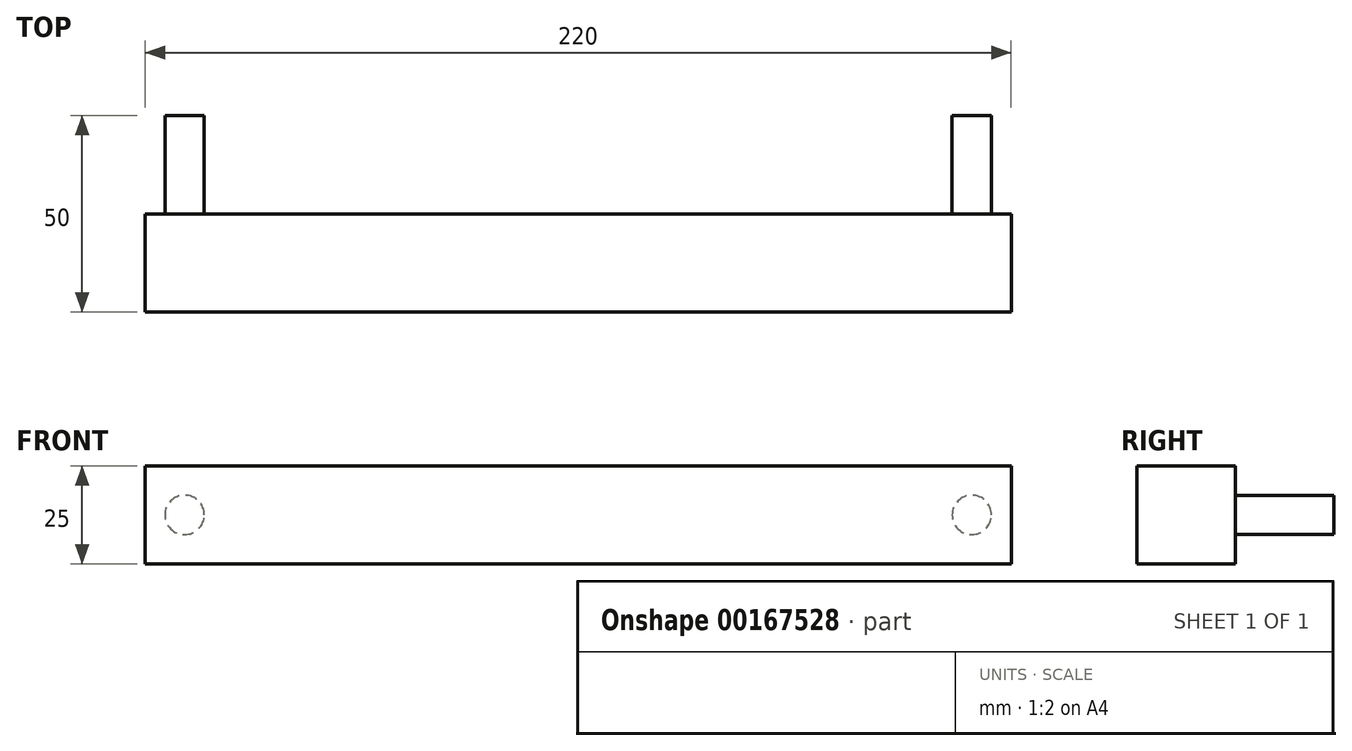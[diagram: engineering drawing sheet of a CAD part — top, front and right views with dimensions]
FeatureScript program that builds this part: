
annotation { "Feature Type Name" : "Feature", "Feature Type Description" : "" }
export const myFeature = defineFeature(function(context is Context, id is Id, definition is map)
    precondition{}
    {
        {
            var Q0;
            Q0=qCreatedBy(makeId("Front.planeOp"),FACE);
            var sketch = newSketch(context, id + "F0", { "sketchPlane" : qUnion([Q0])});
            skLineSegment(sketch, "E0.bottom", {"start": v(-6.67, 0) * mm, "end": v(213.33, 0) * mm});
            skLineSegment(sketch, "E0.top", {"start": v(-6.67, 25) * mm, "end": v(213.33, 25) * mm});
            skLineSegment(sketch, "E0.left", {"start": v(-6.67, 0) * mm, "end": v(-6.67, 25) * mm});
            skLineSegment(sketch, "E0.right", {"start": v(213.33, 0) * mm, "end": v(213.33, 25) * mm});
            skCircle(sketch, "E1", {"center": v(3.33, 12.5) * mm, "radius": 5 * mm});
            skPoint(sketch, "E1.centerSnap0", {"position": v(-6.67, 12.5) * mm});
            skCircle(sketch, "E2", {"center": v(203.33, 12.5) * mm, "radius": 5 * mm});
            skPoint(sketch, "E2.centerSnap0", {"position": v(213.33, 12.5) * mm});
            skSolve(sketch);
        }
        {
            var Q0;
            Q0=makeQuery(id+"F0.imprint","IMPRINT",FACE,{"disambiguationData":[TD([[makeQuery(id+"F0.imprint","IMPRINT",EDGE,{"derivedFrom":sQuery(id+"F0.wireOp",EDGE,"E0.bottom")}),1.0]])]});
            var Q1;
            Q1=makeQuery(id+"F0.imprint","IMPRINT",FACE,{"disambiguationData":[TD([[makeQuery(id+"F0.imprint","IMPRINT",EDGE,{"derivedFrom":sQuery(id+"F0.wireOp",EDGE,"E1")}),1.0]])]});
            var Q2;
            Q2=makeQuery(id+"F0.imprint","IMPRINT",FACE,{"disambiguationData":[TD([[makeQuery(id+"F0.imprint","IMPRINT",EDGE,{"derivedFrom":sQuery(id+"F0.wireOp",EDGE,"E2")}),1.0]])]});
            extrude(context, id + "F1", {"entities" : qUnion([Q0, Q1, Q2]), "depth" : 25 * mm});
        }
        {
            var Q0;
            Q0=makeQuery(id+"F0.imprint","IMPRINT",FACE,{"disambiguationData":[TD([[makeQuery(id+"F0.imprint","IMPRINT",EDGE,{"derivedFrom":sQuery(id+"F0.wireOp",EDGE,"E1")}),1.0]])]});
            var Q1;
            Q1=makeQuery(id+"F0.imprint","IMPRINT",FACE,{"disambiguationData":[TD([[makeQuery(id+"F0.imprint","IMPRINT",EDGE,{"derivedFrom":sQuery(id+"F0.wireOp",EDGE,"E2")}),1.0]])]});
            extrude(context, id + "F2", {"entities" : qUnion([Q0, Q1]), "operationType" : NewBodyOperationType.ADD, "oppositeDirection" : true, "depth" : 25 * mm});
        }
    });
